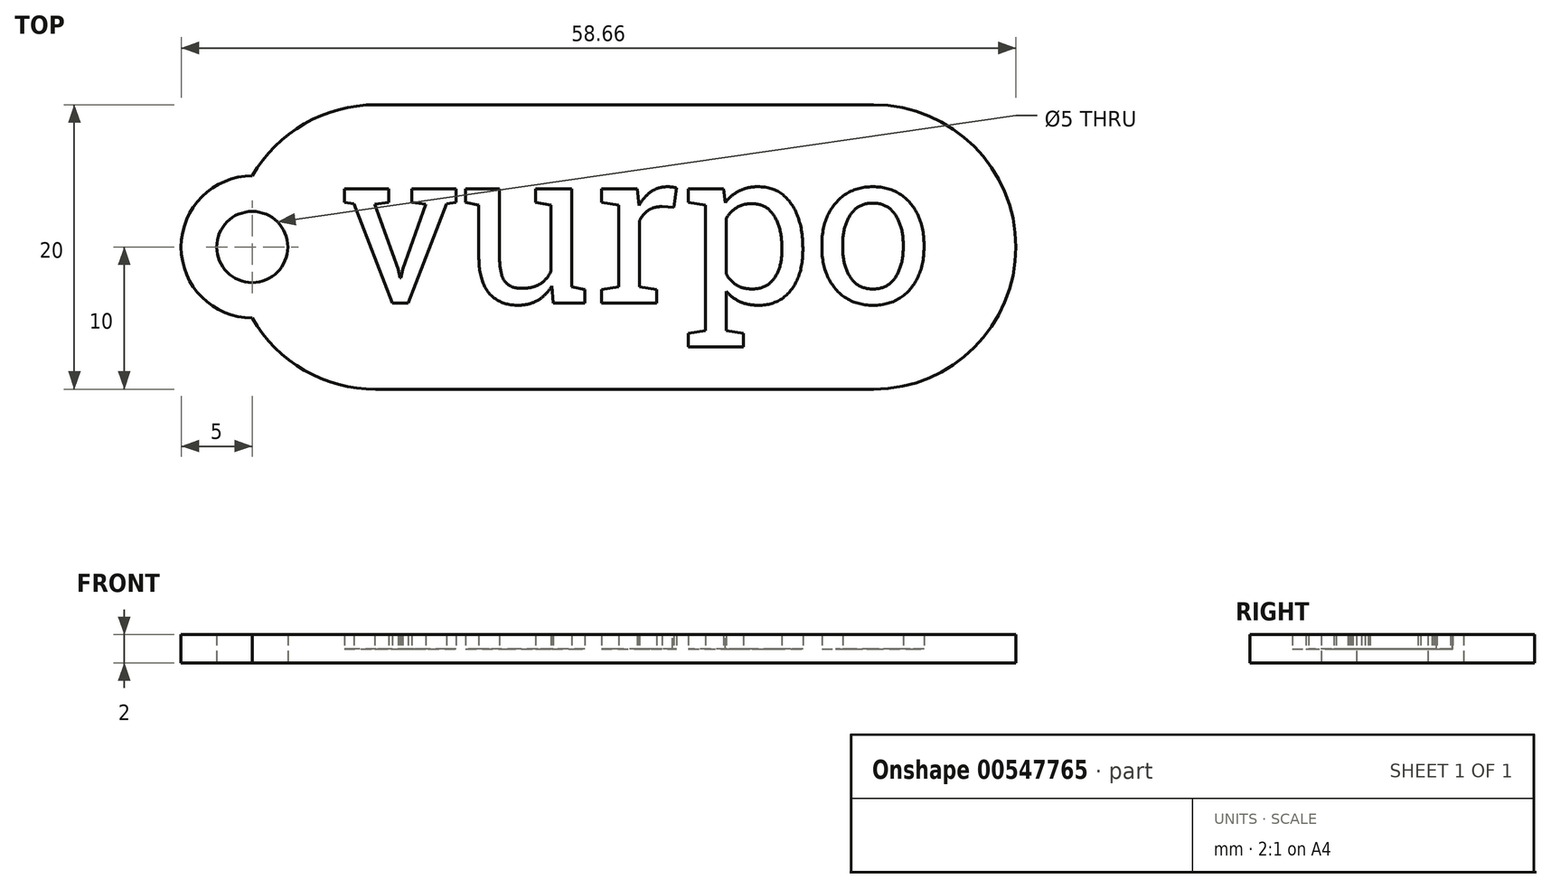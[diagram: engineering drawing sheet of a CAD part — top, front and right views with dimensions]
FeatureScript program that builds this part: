
annotation { "Feature Type Name" : "Feature", "Feature Type Description" : "" }
export const myFeature = defineFeature(function(context is Context, id is Id, definition is map)
    precondition{}
    {
        {
            var Q0;
            Q0=qCreatedBy(makeId("Top.planeOp"),FACE);
            var sketch = newSketch(context, id + "F0", { "sketchPlane" : qUnion([Q0])});
            skLineSegment(sketch, "E0.bottom", {"start": v(17.5, 10) * mm, "end": v(-17.5, 10) * mm});
            skLineSegment(sketch, "E0.top", {"start": v(17.5, -10) * mm, "end": v(-17.5, -10) * mm});
            skLineSegment(sketch, "E0.left", {"start": v(27.5, 0) * mm, "end": v(27.5, 0) * mm});
            skLineSegment(sketch, "E0.right", {"start": v(-27.5, 0) * mm, "end": v(-27.5, 0) * mm});
            skPoint(sketch, "E0.middle", {"position": v(0, 0) * mm});
            skPoint(sketch, "E1.visualSharp", {"position": v(-27.5, 10) * mm});
            skArc(sketch, "E1.filletArc", {"start": v(-17.5, 10) * mm, "mid": v(-24.57, 7.07) * mm, "end": v(-27.5, 0) * mm});
            skPoint(sketch, "E2.visualSharp", {"position": v(-27.5, -10) * mm});
            skArc(sketch, "E2.filletArc", {"start": v(-27.5, 0) * mm, "mid": v(-24.57, -7.07) * mm, "end": v(-17.5, -10) * mm});
            skPoint(sketch, "E3.visualSharp", {"position": v(27.5, -10) * mm});
            skArc(sketch, "E3.filletArc", {"start": v(17.5, -10) * mm, "mid": v(24.57, -7.07) * mm, "end": v(27.5, 0) * mm});
            skPoint(sketch, "E4.visualSharp", {"position": v(27.5, 10) * mm});
            skArc(sketch, "E4.filletArc", {"start": v(27.5, 0) * mm, "mid": v(24.57, 7.07) * mm, "end": v(17.5, 10) * mm});
            skPoint(sketch, "E5", {"position": v(-26.16, 0) * mm});
            skPoint(sketch, "E6", {"position": v(-26.16, 5) * mm});
            skCircle(sketch, "E7", {"center": v(-26.16, 0) * mm, "radius": 5 * mm});
            skCircle(sketch, "E8", {"center": v(-26.16, 0) * mm, "radius": 2.5 * mm});
            skSolve(sketch);
        }
        {
            var Q0;
            {var subQ5=sQuery(id+"F0.wireOp",EDGE,"E0.bottom");Q0=makeQuery(id+"F0.imprint","IMPRINT",FACE,{"disambiguationData":[TD([[makeQuery(id+"F0.imprint","IMPRINT",EDGE,{"derivedFrom":subQ5}),1.0]])]});}
            var Q1;
            {var subQ0=sQuery(id+"F0.wireOp",EDGE,"E7");var subQ1=sQuery(id+"F0.wireOp",EDGE,"E1.filletArc");var subQ2=makeQuery(id+"F0.imprint","INTERSECT",VERTEX,{"derivedFrom":[subQ1,subQ0]});Q1=makeQuery(id+"F0.imprint","IMPRINT",FACE,{"disambiguationData":[TD([[makeQuery(id+"F0.imprint","IMPRINT",EDGE,{"disambiguationData":[TD([[subQ2,-1.0]])],"derivedFrom":subQ1}),1.0]])]});}
            var Q2;
            {var subQ0=sQuery(id+"F0.wireOp",EDGE,"E7");var subQ1=sQuery(id+"F0.wireOp",EDGE,"E1.filletArc");var subQ2=makeQuery(id+"F0.imprint","INTERSECT",VERTEX,{"derivedFrom":[subQ1,subQ0]});Q2=makeQuery(id+"F0.imprint","IMPRINT",FACE,{"disambiguationData":[TD([[makeQuery(id+"F0.imprint","IMPRINT",EDGE,{"disambiguationData":[TD([[subQ2,-1.0]])],"derivedFrom":subQ1}),-1.0]])]});}
            extrude(context, id + "F1", {"entities" : qUnion([Q0, Q1, Q2]), "depth" : 1 * mm, "offsetDistance" : 25 * mm});
        }
        {
            var Q0;
            Q0=makeQuery(id+"F1.opExtrude","CAP_FACE",FACE,{"disambiguationData":[OSD([sQuery(id+"F0.wireOp",EDGE,"E0.bottom"),sQuery(id+"F0.wireOp",EDGE,"E0.top"),sQuery(id+"F0.wireOp",EDGE,"E1.filletArc"),sQuery(id+"F0.wireOp",EDGE,"E2.filletArc"),sQuery(id+"F0.wireOp",EDGE,"E3.filletArc"),sQuery(id+"F0.wireOp",EDGE,"E4.filletArc"),sQuery(id+"F0.wireOp",EDGE,"E7"),sQuery(id+"F0.wireOp",EDGE,"E8")])],"isStart":false});
            var sketch = newSketch(context, id + "F2", { "sketchPlane" : qUnion([Q0])});
            skText(sketch, "E9", { "text": "vurpo", "fontName": "RobotoSlab-Regular.ttf"});
            skPoint(sketch, "E10", {"position": v(-23.03, 0) * mm});
            const initialGuessF2  = {"E9": [-0.02, -0.00394, 1, 0, 0.01094]};
            skSetInitialGuess(sketch, initialGuessF2);
            skSolve(sketch);
        }
        {
            var Q0;
            Q0=makeQuery(id+"F2.imprint","IMPRINT",FACE,{"disambiguationData":[TD([[makeQuery(id+"F2.imprint","IMPRINT",EDGE,{"derivedFrom":sQuery(id+"F2.wireOp",EDGE,"E9.sketch_text.stroke-0")}),1.0]])]});
            var Q1;
            Q1=makeQuery(id+"F2.imprint","IMPRINT",FACE,{"disambiguationData":[TD([[makeQuery(id+"F2.imprint","IMPRINT",EDGE,{"derivedFrom":sQuery(id+"F2.wireOp",EDGE,"E9.sketch_text.stroke-81")}),1.0]])]});
            var Q2;
            Q2=makeQuery(id+"F2.imprint","IMPRINT",FACE,{"disambiguationData":[TD([[makeQuery(id+"F2.imprint","IMPRINT",EDGE,{"derivedFrom":sQuery(id+"F2.wireOp",EDGE,"E9.sketch_text.stroke-101")}),1.0]])]});
            extrude(context, id + "F3", {"entities" : qUnion([Q0, Q1, Q2]), "operationType" : NewBodyOperationType.ADD, "depth" : 1 * mm, "offsetDistance" : 25 * mm});
        }
    });
